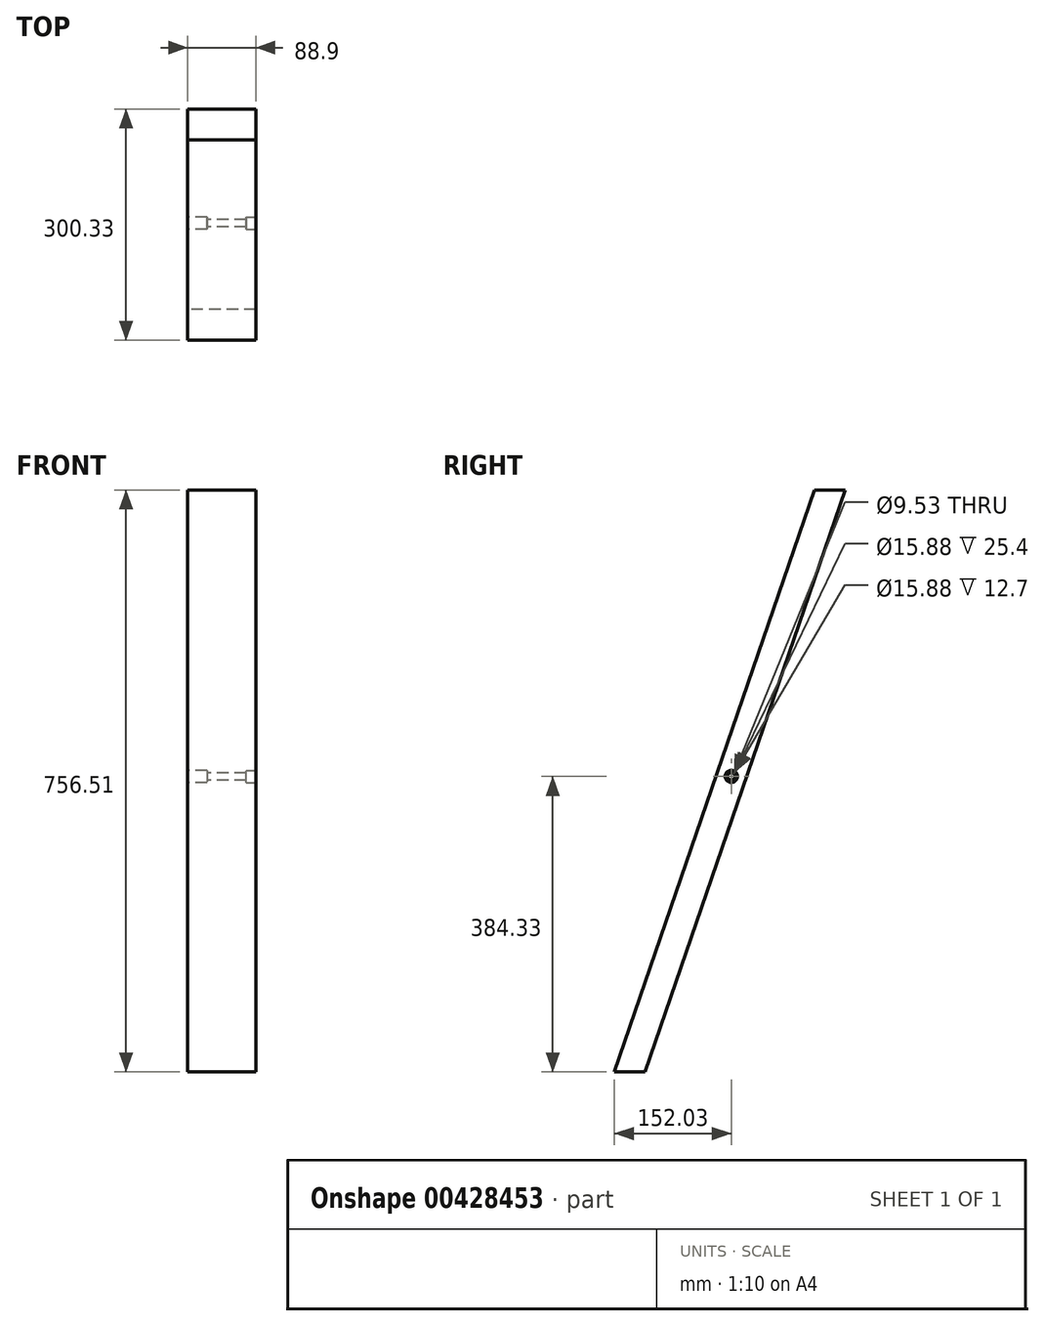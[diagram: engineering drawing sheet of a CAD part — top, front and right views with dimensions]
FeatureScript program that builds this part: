
annotation { "Feature Type Name" : "Feature", "Feature Type Description" : "" }
export const myFeature = defineFeature(function(context is Context, id is Id, definition is map)
    precondition{}
    {
        {
            var Q0;
            Q0=qCreatedBy(makeId("Right.planeOp"),FACE);
            var sketch = newSketch(context, id + "F0", { "sketchPlane" : qUnion([Q0])});
            skLineSegment(sketch, "E0", {"start": v(-44.44, -23) * mm, "end": v(-304.93, -779.52) * mm});
            skLineSegment(sketch, "E1", {"start": v(-4.6, -23) * mm, "end": v(-265.09, -779.52) * mm});
            skLineSegment(sketch, "E2", {"start": v(-44.44, -23) * mm, "end": v(-4.6, -23) * mm});
            skLineSegment(sketch, "E3", {"start": v(-304.93, -779.52) * mm, "end": v(-265.09, -779.52) * mm});
            skSolve(sketch);
        }
        {
            var Q0;
            Q0 = qSketchRegion(id + "F0", true);
            extrude(context, id + "F1", {"entities" : qUnion([Q0]), "depth" : 44.45 * mm, "hasSecondDirection" : true, "secondDirectionOppositeDirection" : true, "secondDirectionDepth" : 44.45 * mm});
        }
        {
            var Q0;
            Q0=makeQuery(id+"F1.opExtrude","CAP_FACE",FACE,{"disambiguationData":[OSD([sQuery(id+"F0.wireOp",EDGE,"E0"),sQuery(id+"F0.wireOp",EDGE,"E1"),sQuery(id+"F0.wireOp",EDGE,"E2"),sQuery(id+"F0.wireOp",EDGE,"E3")])],"isStart":true});
            var sketch = newSketch(context, id + "F2", { "sketchPlane" : qUnion([Q0])});
            skPoint(sketch, "E4", {"position": v(152.9, -395.19) * mm});
            skSolve(sketch);
        }
        {
            var Q0;
            Q0=sQuery(id+"F2.wireOp",VERTEX,"E4");
            var Q1;
            Q1=makeQuery(id+"F1.opExtrude","SWEPT_BODY",BODY,{"disambiguationData":[OSD([sQuery(id+"F0.wireOp",EDGE,"E0"),sQuery(id+"F0.wireOp",EDGE,"E1"),sQuery(id+"F0.wireOp",EDGE,"E2"),sQuery(id+"F0.wireOp",EDGE,"E3")])]});
            hole(context, id + "F3", {"style" : HoleStyle.C_BORE, "endStyle" : HoleEndStyle.BLIND, "holeDiameter" : 9.52 * mm, "cBoreDiameter" : 15.88 * mm, "cBoreDepth" : 25.4 * mm, "holeDepth" : 31.75 * mm, "isTappedThrough" : true, "tappedDepth" : 12.7 * mm, "tapClearance" : 3, "startFromSketch" : true, "locations" : qUnion([Q0]), "scope" : qUnion([Q1])});
        }
        {
            var Q0;
            Q0=makeQuery(id+"F1.opExtrude","CAP_FACE",FACE,{"disambiguationData":[OSD([sQuery(id+"F0.wireOp",EDGE,"E0"),sQuery(id+"F0.wireOp",EDGE,"E1"),sQuery(id+"F0.wireOp",EDGE,"E2"),sQuery(id+"F0.wireOp",EDGE,"E3")])],"isStart":false});
            var sketch = newSketch(context, id + "F4", { "sketchPlane" : qUnion([Q0])});
            skPoint(sketch, "E5", {"position": v(-152.9, -395.19) * mm});
            skSolve(sketch);
        }
        {
            var Q0;
            Q0=sQuery(id+"F4.wireOp",VERTEX,"E5");
            var Q1;
            Q1=makeQuery(id+"F1.opExtrude","SWEPT_BODY",BODY,{"disambiguationData":[OSD([sQuery(id+"F0.wireOp",EDGE,"E0"),sQuery(id+"F0.wireOp",EDGE,"E1"),sQuery(id+"F0.wireOp",EDGE,"E2"),sQuery(id+"F0.wireOp",EDGE,"E3")])]});
            hole(context, id + "F5", {"style" : HoleStyle.C_BORE, "endStyle" : HoleEndStyle.THROUGH, "holeDiameter" : 9.52 * mm, "cBoreDiameter" : 15.88 * mm, "cBoreDepth" : 12.7 * mm, "isTappedThrough" : true, "tappedDepth" : 12.7 * mm, "tapClearance" : 3, "startFromSketch" : true, "locations" : qUnion([Q0]), "scope" : qUnion([Q1])});
        }
    });
